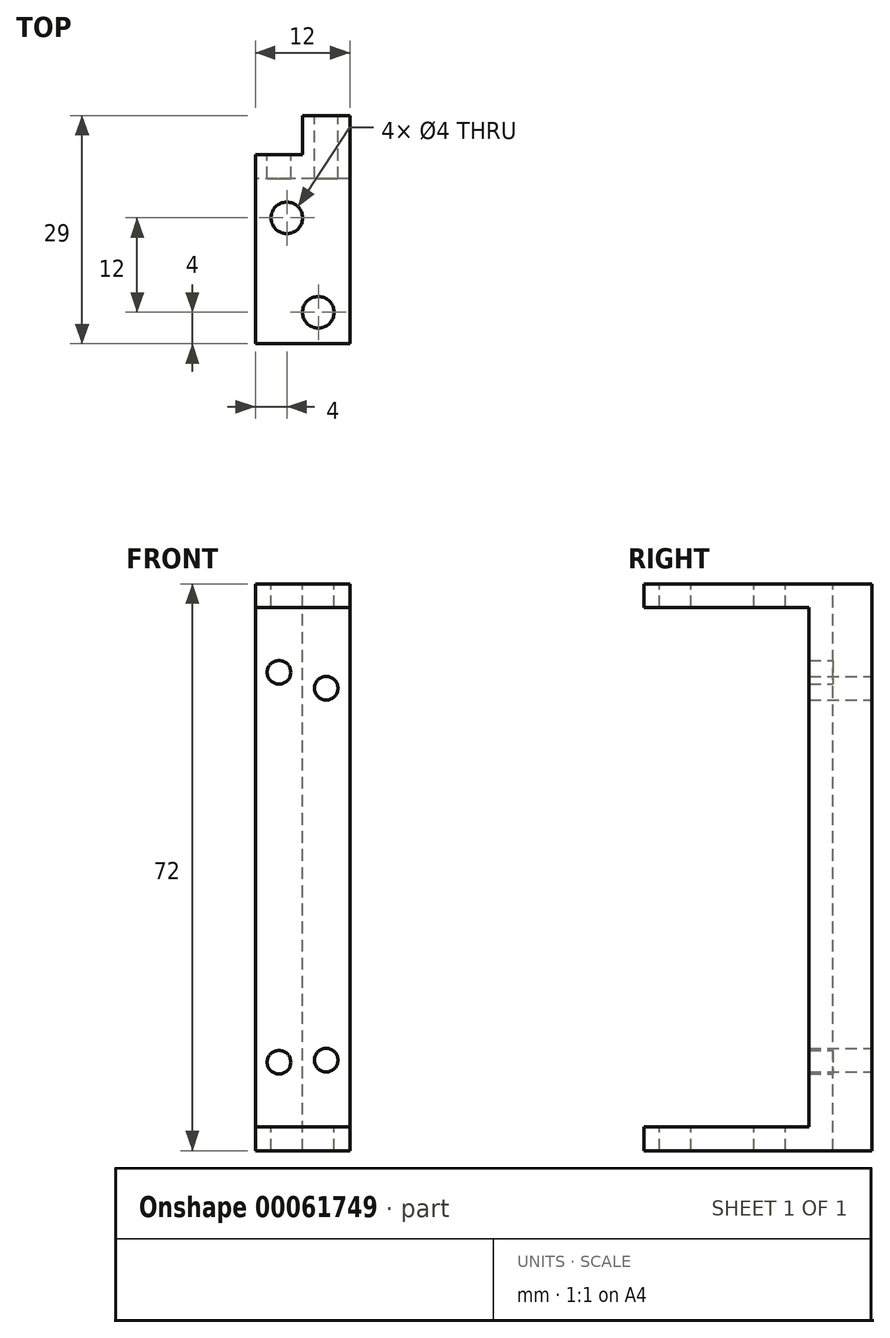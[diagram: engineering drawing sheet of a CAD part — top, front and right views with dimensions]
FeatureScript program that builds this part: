
annotation { "Feature Type Name" : "Feature", "Feature Type Description" : "" }
export const myFeature = defineFeature(function(context is Context, id is Id, definition is map)
    precondition{}
    {
        {
            var Q0;
            Q0=qCreatedBy(makeId("Right.planeOp"),FACE);
            var sketch = newSketch(context, id + "F0", { "sketchPlane" : qUnion([Q0])});
            skLineSegment(sketch, "E0", {"start": v(-10.5, 37.5) * mm, "end": v(18.5, 37.5) * mm});
            skLineSegment(sketch, "E1", {"start": v(18.5, 37.5) * mm, "end": v(18.5, -34.5) * mm});
            skLineSegment(sketch, "E2.0", {"start": v(10.5, 34.5) * mm, "end": v(10.5, -34.5) * mm});
            skLineSegment(sketch, "E2.1", {"start": v(-10.5, 34.5) * mm, "end": v(10.5, 34.5) * mm});
            skLineSegment(sketch, "E3", {"start": v(-10.5, 37.5) * mm, "end": v(-10.5, 34.5) * mm});
            skLineSegment(sketch, "E4", {"start": v(18.5, -34.5) * mm, "end": v(10.5, -34.5) * mm});
            skLineSegment(sketch, "E5", {"start": v(10.5, 0) * mm, "end": v(-14.36, 0) * mm, "construction": true});
            skLineSegment(sketch, "E6", {"start": v(0, 34.5) * mm, "end": v(0, -1.72) * mm, "construction": true});
            skSolve(sketch);
        }
        {
            var Q0;
            Q0=makeQuery(id+"F0.imprint","IMPRINT",FACE,{"disambiguationData":[TD([[makeQuery(id+"F0.imprint","IMPRINT",EDGE,{"derivedFrom":sQuery(id+"F0.wireOp",EDGE,"E0")}),-1.0]])]});
            extrude(context, id + "F1", {"entities" : qUnion([Q0]), "depth" : 12 * mm});
        }
        {
            var Q0;
            Q0=makeQuery(id+"F1.opExtrude","SWEPT_FACE",FACE,{"disambiguationData":[OSD([sQuery(id+"F0.wireOp",EDGE,"E0")])]});
            var sketch = newSketch(context, id + "F2", { "sketchPlane" : qUnion([Q0])});
            skLineSegment(sketch, "E7.bottom", {"start": v(0, 18.5) * mm, "end": v(6.02, 18.5) * mm});
            skLineSegment(sketch, "E7.top", {"start": v(0, 13.5) * mm, "end": v(6.02, 13.5) * mm});
            skLineSegment(sketch, "E7.left", {"start": v(0, 18.5) * mm, "end": v(0, 13.5) * mm});
            skLineSegment(sketch, "E7.right", {"start": v(6.02, 18.5) * mm, "end": v(6.02, 13.5) * mm});
            skSolve(sketch);
        }
        {
            var Q0;
            Q0=makeQuery(id+"F2.imprint","IMPRINT",FACE,{"disambiguationData":[TD([[makeQuery(id+"F2.imprint","IMPRINT",EDGE,{"derivedFrom":sQuery(id+"F2.wireOp",EDGE,"E7.bottom")}),1.0]])]});
            extrude(context, id + "F3", {"entities" : qUnion([Q0]), "operationType" : NewBodyOperationType.REMOVE, "oppositeDirection" : true, "depth" : 72 * mm});
        }
        {
            var Q0;
            Q0=makeQuery(id+"F1.opExtrude","SWEPT_FACE",FACE,{"disambiguationData":[OSD([sQuery(id+"F0.wireOp",EDGE,"E1")])]});
            var sketch = newSketch(context, id + "F4", { "sketchPlane" : qUnion([Q0])});
            skCircle(sketch, "E8", {"center": v(-9, 24.25) * mm, "radius": 1.5 * mm});
            skCircle(sketch, "E9", {"center": v(-9, -23) * mm, "radius": 1.5 * mm});
            skLineSegment(sketch, "E10", {"start": v(-9, 24.25) * mm, "end": v(-9, -23) * mm, "construction": true});
            skLineSegment(sketch, "E11", {"start": v(-9, 24.25) * mm, "end": v(-9, 37.5) * mm, "construction": true});
            skSolve(sketch);
        }
        {
            var Q0;
            Q0=makeQuery(id+"F4.imprint","IMPRINT",FACE,{"disambiguationData":[TD([[makeQuery(id+"F4.imprint","IMPRINT",EDGE,{"derivedFrom":sQuery(id+"F4.wireOp",EDGE,"E8")}),1.0]])]});
            var Q1;
            Q1=makeQuery(id+"F4.imprint","IMPRINT",FACE,{"disambiguationData":[TD([[makeQuery(id+"F4.imprint","IMPRINT",EDGE,{"derivedFrom":sQuery(id+"F4.wireOp",EDGE,"E9")}),1.0]])]});
            extrude(context, id + "F5", {"entities" : qUnion([Q0, Q1]), "operationType" : NewBodyOperationType.REMOVE, "oppositeDirection" : true, "depth" : 25 * mm});
        }
        {
            var Q0;
            Q0=makeQuery(id+"F3.boolean.opBoolean","COPY",FACE,{"derivedFrom":makeQuery(id+"F3.opExtrude","SWEPT_FACE",FACE,{"disambiguationData":[OSD([sQuery(id+"F2.wireOp",EDGE,"E7.top")])]})});
            var sketch = newSketch(context, id + "F6", { "sketchPlane" : qUnion([Q0])});
            skCircle(sketch, "E12", {"center": v(-3, 26.27) * mm, "radius": 1.5 * mm});
            skCircle(sketch, "E13", {"center": v(-3, -23.27) * mm, "radius": 1.5 * mm});
            skLineSegment(sketch, "E14", {"start": v(-3, 26.27) * mm, "end": v(-3, -23.27) * mm, "construction": true});
            skPoint(sketch, "E15", {"position": v(-3, 37.5) * mm});
            skSolve(sketch);
        }
        {
            var Q0;
            Q0=makeQuery(id+"F6.imprint","IMPRINT",FACE,{"disambiguationData":[TD([[makeQuery(id+"F6.imprint","IMPRINT",EDGE,{"derivedFrom":sQuery(id+"F6.wireOp",EDGE,"E13")}),1.0]])]});
            var Q1;
            Q1=makeQuery(id+"F6.imprint","IMPRINT",FACE,{"disambiguationData":[TD([[makeQuery(id+"F6.imprint","IMPRINT",EDGE,{"derivedFrom":sQuery(id+"F6.wireOp",EDGE,"E12")}),1.0]])]});
            extrude(context, id + "F7", {"entities" : qUnion([Q0, Q1]), "operationType" : NewBodyOperationType.REMOVE, "oppositeDirection" : true, "depth" : 25 * mm});
        }
        {
            var Q0;
            Q0=makeQuery(id+"F1.opExtrude","SWEPT_FACE",FACE,{"disambiguationData":[OSD([sQuery(id+"F0.wireOp",EDGE,"E2.0")])]});
            var sketch = newSketch(context, id + "F8", { "sketchPlane" : qUnion([Q0])});
            skLineSegment(sketch, "E16.bottom", {"start": v(0, -34.5) * mm, "end": v(12, -34.5) * mm});
            skLineSegment(sketch, "E16.top", {"start": v(0, -31.5) * mm, "end": v(12, -31.5) * mm});
            skLineSegment(sketch, "E16.left", {"start": v(0, -31.5) * mm, "end": v(0, -34.5) * mm});
            skLineSegment(sketch, "E16.right", {"start": v(12, -31.5) * mm, "end": v(12, -34.5) * mm});
            skSolve(sketch);
        }
        {
            var Q0;
            Q0=makeQuery(id+"F8.imprint","IMPRINT",FACE,{"disambiguationData":[TD([[makeQuery(id+"F8.imprint","IMPRINT",EDGE,{"derivedFrom":sQuery(id+"F8.wireOp",EDGE,"E16.bottom")}),-1.0]])]});
            extrude(context, id + "F9", {"entities" : qUnion([Q0]), "operationType" : NewBodyOperationType.ADD, "depth" : 21 * mm});
        }
        {
            var Q0;
            Q0=makeQuery(id+"F1.opExtrude","SWEPT_FACE",FACE,{"disambiguationData":[OSD([sQuery(id+"F0.wireOp",EDGE,"E0")])]});
            var sketch = newSketch(context, id + "F10", { "sketchPlane" : qUnion([Q0])});
            skCircle(sketch, "E17", {"center": v(4, 5.5) * mm, "radius": 2 * mm});
            skCircle(sketch, "E18", {"center": v(8, -6.5) * mm, "radius": 2 * mm});
            skSolve(sketch);
        }
        {
            var Q0;
            Q0=makeQuery(id+"F10.imprint","IMPRINT",FACE,{"disambiguationData":[TD([[makeQuery(id+"F10.imprint","IMPRINT",EDGE,{"derivedFrom":sQuery(id+"F10.wireOp",EDGE,"E17")}),1.0]])]});
            var Q1;
            Q1=makeQuery(id+"F10.imprint","IMPRINT",FACE,{"disambiguationData":[TD([[makeQuery(id+"F10.imprint","IMPRINT",EDGE,{"derivedFrom":sQuery(id+"F10.wireOp",EDGE,"E18")}),1.0]])]});
            extrude(context, id + "F11", {"entities" : qUnion([Q0, Q1]), "operationType" : NewBodyOperationType.REMOVE, "oppositeDirection" : true, "depth" : 72 * mm});
        }
    });
